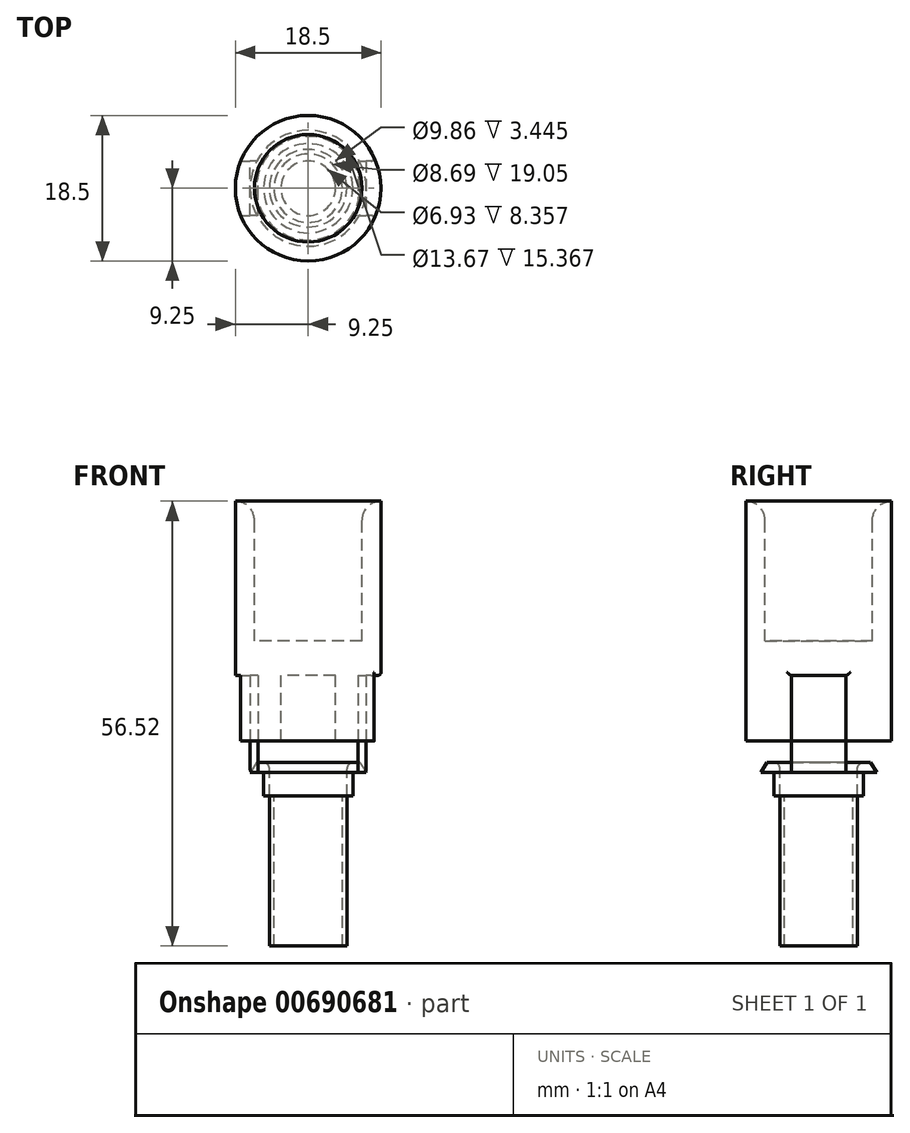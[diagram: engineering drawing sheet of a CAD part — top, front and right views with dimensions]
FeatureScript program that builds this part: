
annotation { "Feature Type Name" : "Feature", "Feature Type Description" : "" }
export const myFeature = defineFeature(function(context is Context, id is Id, definition is map)
    precondition{}
    {
        {
            var Q0;
            Q0=qCreatedBy(makeId("Front.planeOp"),FACE);
            var sketch = newSketch(context, id + "F0", { "sketchPlane" : qUnion([Q0])});
            skLineSegment(sketch, "E0.bottom", {"start": v(0, 0) * mm, "end": v(9.25, 0) * mm});
            skLineSegment(sketch, "E0.left", {"start": v(0, 0) * mm, "end": v(0, 30.48) * mm, "construction": true});
            skPoint(sketch, "E1", {"position": v(9.25, 0) * mm});
            skPoint(sketch, "E2", {"position": v(9.25, 30.48) * mm});
            skLineSegment(sketch, "E3", {"start": v(9.25, 0) * mm, "end": v(9.25, 30.48) * mm});
            skLineSegment(sketch, "E4", {"start": v(9.25, 30.48) * mm, "end": v(9.25, 30.48) * mm});
            skLineSegment(sketch, "E5", {"start": v(6.83, 28.07) * mm, "end": v(6.83, 12.7) * mm});
            skLineSegment(sketch, "E6", {"start": v(6.83, 12.7) * mm, "end": v(0, 12.7) * mm});
            skPoint(sketch, "E7.visualSharp", {"position": v(6.83, 30.48) * mm});
            skArc(sketch, "E7.filletArc", {"start": v(9.25, 30.48) * mm, "mid": v(7.54, 29.77) * mm, "end": v(6.83, 28.07) * mm});
            skLineSegment(sketch, "E8", {"start": v(0, 12.7) * mm, "end": v(0, 0) * mm});
            skLineSegment(sketch, "E9", {"start": v(0, -6.99) * mm, "end": v(4.93, -6.99) * mm, "construction": true});
            skLineSegment(sketch, "E10", {"start": v(4.93, -6.99) * mm, "end": v(5.66, -6.99) * mm});
            skLineSegment(sketch, "E11", {"start": v(5.66, -6.99) * mm, "end": v(5.66, -3.96) * mm});
            skLineSegment(sketch, "E12", {"start": v(5.66, -3.96) * mm, "end": v(7.37, -3.96) * mm});
            skLineSegment(sketch, "E13", {"start": v(7.37, -3.96) * mm, "end": v(6.58, -2.72) * mm});
            skLineSegment(sketch, "E14", {"start": v(6.58, -2.72) * mm, "end": v(5.75, -2.72) * mm});
            skLineSegment(sketch, "E15", {"start": v(4.93, -3.54) * mm, "end": v(4.93, -6.99) * mm});
            skLineSegment(sketch, "E16", {"start": v(0, 0) * mm, "end": v(0, -0.25) * mm, "construction": true});
            skLineSegment(sketch, "E17", {"start": v(0, 0) * mm, "end": v(0, -9.73) * mm, "construction": true});
            skPoint(sketch, "E18.visualSharp", {"position": v(4.93, -2.72) * mm});
            skArc(sketch, "E18.filletArc", {"start": v(5.75, -2.72) * mm, "mid": v(5.17, -2.96) * mm, "end": v(4.93, -3.54) * mm});
            skLineSegment(sketch, "E19.bottom", {"start": v(-3.47, 8.36) * mm, "end": v(3.47, 8.36) * mm});
            skLineSegment(sketch, "E19.top", {"start": v(-3.47, -3.96) * mm, "end": v(3.47, -3.96) * mm});
            skLineSegment(sketch, "E19.left", {"start": v(-3.47, 8.36) * mm, "end": v(-3.47, -3.96) * mm});
            skLineSegment(sketch, "E19.right", {"start": v(3.47, 8.36) * mm, "end": v(3.47, -3.96) * mm});
            skPoint(sketch, "E19.middle", {"position": v(0, 2.2) * mm});
            skSolve(sketch);
        }
        {
            var Q0;
            {var subQ1=sQuery(id+"F0.wireOp",EDGE,"E3");Q0=makeQuery(id+"F0.imprint","IMPRINT",FACE,{"disambiguationData":[TD([[makeQuery(id+"F0.imprint","IMPRINT",EDGE,{"derivedFrom":subQ1}),1.0]])]});}
            var Q1;
            Q1=makeQuery(id+"F0.imprint","IMPRINT",FACE,{"disambiguationData":[TD([[makeQuery(id+"F0.imprint","IMPRINT",EDGE,{"derivedFrom":sQuery(id+"F0.wireOp",EDGE,"E10")}),1.0]])]});
            var Q2;
            Q2=sQuery(id+"F0.wireOp",EDGE,"E8");
            revolve(context, id + "F1", {"surfaceOperationType" : NewSurfaceOperationType.NEW, "entities" : qUnion([Q0, Q1]), "axis" : qUnion([Q2]), "revolveType" : RevolveType.FULL});
        }
        {
            var Q0;
            Q0=qCreatedBy(makeId("Right.planeOp"),FACE);
            cPlane(context, id + "F2", {"entities" : qUnion([Q0]), "cplaneType" : CPlaneType.OFFSET, "offset" : 7.37 * mm, "width" : 152.4 * mm, "height" : 152.4 * mm});
        }
        {
            var Q0;
            Q0=qCreatedBy(id+"F2.planeOp",FACE);
            var sketch = newSketch(context, id + "F3", { "sketchPlane" : qUnion([Q0])});
            skLineSegment(sketch, "E20.bottom", {"start": v(-3.47, 8.36) * mm, "end": v(3.47, 8.36) * mm});
            skLineSegment(sketch, "E20.top", {"start": v(-3.47, -3.96) * mm, "end": v(3.47, -3.96) * mm});
            skLineSegment(sketch, "E20.left", {"start": v(-3.47, 8.36) * mm, "end": v(-3.47, -3.96) * mm});
            skLineSegment(sketch, "E20.right", {"start": v(3.47, 8.36) * mm, "end": v(3.47, -3.96) * mm});
            skPoint(sketch, "E21.0", {"position": v(0, -3.96) * mm});
            skSolve(sketch);
        }
        {
            var Q0;
            Q0 = qSketchRegion(id + "F3", true);
            extrude(context, id + "F4", {"entities" : qUnion([Q0]), "oppositeDirection" : true, "depth" : 1.02 * mm, "offsetDistance" : 25.4 * mm});
        }
        {
            var Q0;
            Q0=makeQuery(id+"F4.opExtrude","CAP_FACE",FACE,{"disambiguationData":[OSD([sQuery(id+"F3.wireOp",EDGE,"E20.bottom"),sQuery(id+"F3.wireOp",EDGE,"E20.top"),sQuery(id+"F3.wireOp",EDGE,"E20.left"),sQuery(id+"F3.wireOp",EDGE,"E20.right")])],"isStart":true});
            var sketch = newSketch(context, id + "F5", { "sketchPlane" : qUnion([Q0])});
            skLineSegment(sketch, "E22", {"start": v(-3.47, 8.36) * mm, "end": v(3.47, 8.36) * mm});
            skLineSegment(sketch, "E23", {"start": v(3.47, 8.36) * mm, "end": v(3.47, 0) * mm});
            skLineSegment(sketch, "E24", {"start": v(3.47, 0) * mm, "end": v(-3.47, 0) * mm});
            skLineSegment(sketch, "E25", {"start": v(-3.47, 0) * mm, "end": v(-3.47, 8.36) * mm});
            skSolve(sketch);
        }
        {
            var Q0;
            Q0 = qSketchRegion(id + "F5", true);
            extrude(context, id + "F6", {"entities" : qUnion([Q0]), "operationType" : NewBodyOperationType.REMOVE, "endBound" : BoundingType.THROUGH_ALL, "depth" : 25.4 * mm, "offsetDistance" : 25.4 * mm});
        }
        {
            var Q0;
            Q0=makeQuery(id+"F6.boolean.opBoolean","INTERSECT",EDGE,{"derivedFrom":[makeQuery(id+"F1.opRevolve","SWEPT_FACE",FACE,{"disambiguationData":[OSD([sQuery(id+"F0.wireOp",EDGE,"E3")])]}),makeQuery(id+"F6.opExtrude","SWEPT_FACE",FACE,{"disambiguationData":[OSD([sQuery(id+"F5.wireOp",EDGE,"E25")])]})]});
            var Q1;
            Q1=makeQuery(id+"F6.boolean.opBoolean","INTERSECT",EDGE,{"derivedFrom":[makeQuery(id+"F1.opRevolve","SWEPT_FACE",FACE,{"disambiguationData":[OSD([sQuery(id+"F0.wireOp",EDGE,"E3")])]}),makeQuery(id+"F6.opExtrude","SWEPT_FACE",FACE,{"disambiguationData":[OSD([sQuery(id+"F5.wireOp",EDGE,"E23")])]})]});
            var Q2;
            Q2=makeQuery(id+"F6.boolean.opBoolean","INTERSECT",EDGE,{"derivedFrom":[makeQuery(id+"F1.opRevolve","SWEPT_FACE",FACE,{"disambiguationData":[OSD([sQuery(id+"F0.wireOp",EDGE,"E3")])]}),makeQuery(id+"F6.opExtrude","SWEPT_FACE",FACE,{"disambiguationData":[OSD([sQuery(id+"F5.wireOp",EDGE,"E22")])]})]});
            fillet(context, id + "F7", {"entities" : qUnion([Q0, Q1, Q2]), "radius" : 0.38 * mm, "tangentPropagation" : true, "allowEdgeOverflow" : false});
        }
        {
            var Q0;
            Q0=makeQuery(id+"F4.opExtrude","CAP_EDGE",EDGE,{"disambiguationData":[OSD([sQuery(id+"F3.wireOp",EDGE,"E20.top")])],"isStart":true});
            fillet(context, id + "F8", {"entities" : qUnion([Q0]), "radius" : 0.38 * mm, "tangentPropagation" : true, "allowEdgeOverflow" : false});
        }
        {
            var Q0;
            Q0=makeQuery(id+"F4.opExtrude","SWEPT_BODY",BODY,{"disambiguationData":[OSD([sQuery(id+"F3.wireOp",EDGE,"E20.bottom"),sQuery(id+"F3.wireOp",EDGE,"E20.top"),sQuery(id+"F3.wireOp",EDGE,"E20.left"),sQuery(id+"F3.wireOp",EDGE,"E20.right")])]});
            var Q1;
            Q1=qCreatedBy(makeId("Front.planeOp"),FACE);
            mirror(context, id + "F9", {"entities" : qUnion([Q0]), "mirrorPlane" : qUnion([Q1])});
        }
        {
            var Q0;
            Q0=makeQuery(id+"F4.opExtrude","SWEPT_BODY",BODY,{"disambiguationData":[OSD([sQuery(id+"F3.wireOp",EDGE,"E20.bottom"),sQuery(id+"F3.wireOp",EDGE,"E20.top"),sQuery(id+"F3.wireOp",EDGE,"E20.left"),sQuery(id+"F3.wireOp",EDGE,"E20.right")])]});
            var Q1;
            Q1=qCreatedBy(makeId("Right.planeOp"),FACE);
            mirror(context, id + "F10", {"entities" : qUnion([Q0]), "mirrorPlane" : qUnion([Q1])});
        }
        {
            var Q0;
            Q0=makeQuery(id+"F10.opPattern","COPY",FACE,{"derivedFrom":makeQuery(id+"F4.opExtrude","CAP_FACE",FACE,{"disambiguationData":[OSD([sQuery(id+"F3.wireOp",EDGE,"E20.bottom"),sQuery(id+"F3.wireOp",EDGE,"E20.top"),sQuery(id+"F3.wireOp",EDGE,"E20.left"),sQuery(id+"F3.wireOp",EDGE,"E20.right")])],"isStart":true}),"instanceName":"1"});
            extrude(context, id + "F11", {"entities" : qUnion([Q0]), "operationType" : NewBodyOperationType.REMOVE, "endBound" : BoundingType.THROUGH_ALL, "depth" : 25.4 * mm, "offsetDistance" : 25.4 * mm});
        }
        {
            var Q0;
            Q0=makeQuery(id+"F1.opRevolve","SWEPT_FACE",FACE,{"disambiguationData":[OSD([sQuery(id+"F0.wireOp",EDGE,"E10")])]});
            var sketch = newSketch(context, id + "F12", { "sketchPlane" : qUnion([Q0])});
            skCircle(sketch, "E26.0", {"center": v(0, 0) * mm, "radius": 4.93 * mm});
            skArc(sketch, "E27.0", {"start": v(1.02, 2.71) * mm, "mid": v(0, 2.9) * mm, "end": v(-1.02, 2.71) * mm});
            skLineSegment(sketch, "E27.1", {"start": v(1.02, -2.71) * mm, "end": v(1.02, 2.71) * mm});
            skArc(sketch, "E27.2", {"start": v(-1.02, -2.71) * mm, "mid": v(0, -2.9) * mm, "end": v(1.02, -2.71) * mm});
            skLineSegment(sketch, "E27.3", {"start": v(-1.02, 2.71) * mm, "end": v(-1.02, -2.71) * mm});
            skCircle(sketch, "E28.0", {"center": v(0, 0) * mm, "radius": 5.56 * mm});
            skCircle(sketch, "E29.0", {"center": v(0, 0) * mm, "radius": 4.34 * mm});
            skSolve(sketch);
        }
        {
            var Q0;
            Q0=makeQuery(id+"F12.imprint","IMPRINT",FACE,{"disambiguationData":[TD([[makeQuery(id+"F12.imprint","IMPRINT",EDGE,{"derivedFrom":sQuery(id+"F12.wireOp",EDGE,"E26.0")}),-1.0]])]});
            extrude(context, id + "F13", {"entities" : qUnion([Q0]), "depth" : 19.05 * mm, "offsetDistance" : 25.4 * mm});
        }
    });
